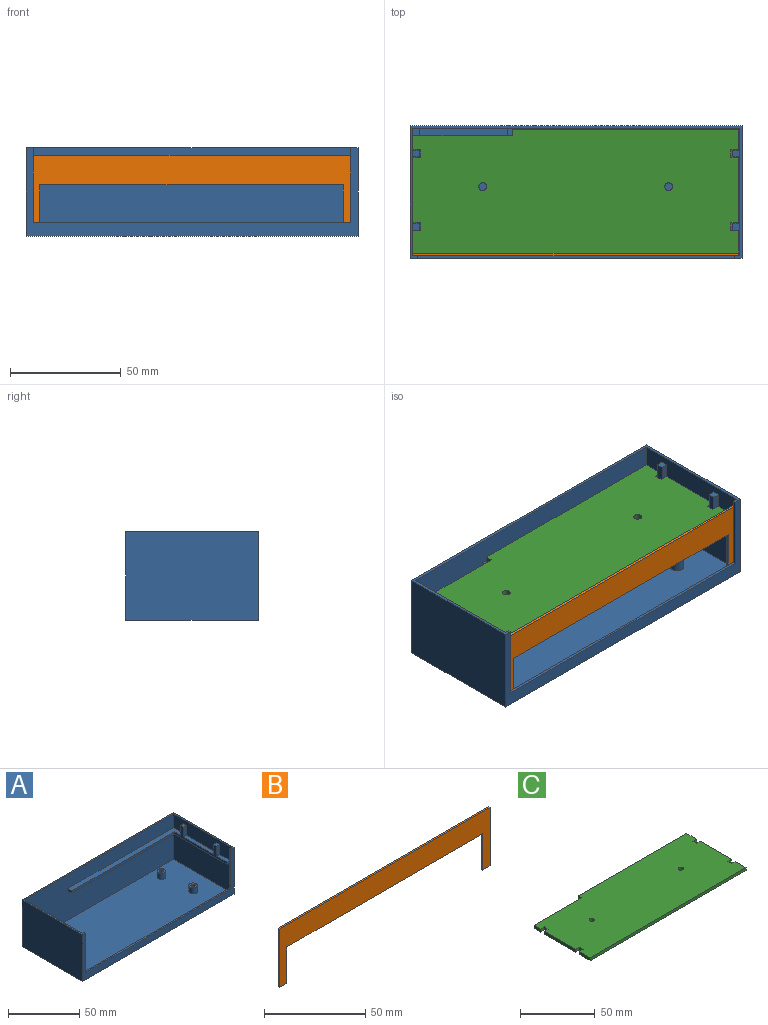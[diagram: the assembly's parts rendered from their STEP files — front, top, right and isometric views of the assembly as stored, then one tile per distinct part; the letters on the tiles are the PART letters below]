
ASSEMBLY  parts=3 mates=4
PART A: 56 faces, bbox 150x60x40 mm
  f0: plane 147.6x57.6mm, normal (0,0,1), area 8388.7mm2, adj f4,f6,f13,f16,f18,f22,f26,f30
  f1: plane 30x3mm, normal (0,0,1), area 90mm2, adj f16,f39,f47,f50
  f2: plane 104.6x10mm, normal (0,0,1), area 436.4mm2, adj f6,f16,f39,f48,f53,f54
  f3: plane 30x3mm, normal (0,0,1), area 90mm2, adj f4,f35,f42,f44
  f4: plane 57.6x38.8mm, normal (1,0,0), area 2071.7mm2, adj f0,f3,f5,f6,f11,f13,f33,f34
  f5: plane 10x3mm, normal (0,0,1), area 30mm2, adj f4,f6,f35,f41
  f6: plane 147.6x38.8mm, normal (0,-1,0), area 5511.7mm2, adj f0,f2,f4,f5,f11,f16,f33,f35
  f7: plane 150x40mm, normal (0,-1,0), area 1146.3mm2, adj f8,f10,f11,f12,f14,f15,f55
  f8: plane 60x40mm, normal (1,0,0), area 2400mm2, adj f7,f9,f11,f12
  f9: plane 150x40mm, normal (0,1,0), area 6000mm2, adj f8,f10,f11,f12
  f10: plane 60x40mm, normal (-1,0,0), area 2400mm2, adj f7,f9,f11,f12
  f11: plane 150x60mm, normal (0,0,1), area 325.9mm2, adj f4,f6,f7,f8,f9,f10,f13,f14
  f12: plane 150x60mm, normal (0,0,-1), area 9000mm2, adj f7,f8,f9,f10
  f13: plane 147.6x38.8mm, normal (0,1,0), area 873.2mm2, adj f0,f4,f11,f14,f15,f16,f55
  f14: plane 33.8x1.2mm, normal (1,0,0), area 40.6mm2, adj f7,f11,f13,f55
  f15: plane 33.8x1.2mm, normal (-1,0,0), area 40.6mm2, adj f7,f11,f13,f55
  f16: plane 57.6x38.8mm, normal (-1,0,0), area 2071.7mm2, adj f0,f1,f2,f6,f11,f13,f37,f38
  f17: cylinder r=1.5mm len=5mm, axis (0,0,-1), area 47.1mm2, adj f19,f20
  f18: cylinder r=3mm len=6mm, axis (0,0,-1), area 94.2mm2, adj f0,f19
  f19: plane 6x6mm, normal (0,0,1), area 21.2mm2, adj f17,f18
  f20: plane 3x3mm, normal (0,0,1), area 7.1mm2, adj f17
  f21: cylinder r=1.5mm len=5mm, axis (0,0,-1), area 47.1mm2, adj f23,f24
  f22: cylinder r=3mm len=6mm, axis (0,0,-1), area 94.2mm2, adj f0,f23
  f23: plane 6x6mm, normal (0,0,1), area 21.2mm2, adj f21,f22
  f24: plane 3x3mm, normal (0,0,1), area 7.1mm2, adj f21
  f25: cylinder r=1.5mm len=5mm, axis (0,0,-1), area 47.1mm2, adj f27,f28
  f26: cylinder r=3mm len=6mm, axis (0,0,-1), area 94.2mm2, adj f0,f27
  f27: plane 6x6mm, normal (0,0,1), area 21.2mm2, adj f25,f26
  f28: plane 3x3mm, normal (0,0,1), area 7.1mm2, adj f25
  f29: cylinder r=1.5mm len=5mm, axis (0,0,-1), area 47.1mm2, adj f31,f32
  f30: cylinder r=3mm len=6mm, axis (0,0,-1), area 94.2mm2, adj f0,f31
  f31: plane 6x6mm, normal (0,0,1), area 21.2mm2, adj f29,f30
  f32: plane 3x3mm, normal (0,0,1), area 7.1mm2, adj f29
  f33: plane 56.1x3mm, normal (0,0,-1), area 168.3mm2, adj f4,f6,f35,f36
  f34: plane 10.1x3mm, normal (0,0,1), area 30.3mm2, adj f4,f35,f36,f45
  f35: plane 56.1x10.5mm, normal (1,0,0), area 163.2mm2, adj f3,f5,f6,f33,f34,f36,f41,f42
  f36: plane 3x2mm, normal (0,-1,0), area 6mm2, adj f4,f33,f34,f35
  f37: plane 104.6x56.1mm, normal (0,0,-1), area 574.7mm2, adj f6,f16,f38,f39,f53,f54
  f38: plane 3x2mm, normal (0,-1,0), area 6mm2, adj f16,f37,f39,f40
  f39: plane 52.1x10.5mm, normal (-1,0,0), area 155.2mm2, adj f1,f2,f37,f38,f40,f47,f48,f49
  f40: plane 10.1x3mm, normal (0,0,1), area 30.3mm2, adj f16,f38,f39,f51
  f41: plane 8.5x3mm, normal (0,1,0), area 25.5mm2, adj f4,f5,f35,f43
  f42: plane 8.5x3mm, normal (0,-1,0), area 25.5mm2, adj f3,f4,f35,f43
  f43: plane 3x3mm, normal (0,0,1), area 9mm2, adj f4,f35,f41,f42
  f44: plane 8.5x3mm, normal (0,1,0), area 25.5mm2, adj f3,f4,f35,f46
  f45: plane 8.5x3mm, normal (0,-1,0), area 25.5mm2, adj f4,f34,f35,f46
  f46: plane 3x3mm, normal (0,0,1), area 9mm2, adj f4,f35,f44,f45
  f47: plane 8.5x3mm, normal (0,-1,0), area 25.5mm2, adj f1,f16,f39,f49
  f48: plane 8.5x3mm, normal (0,1,0), area 25.5mm2, adj f2,f16,f39,f49
  f49: plane 3x3mm, normal (0,0,1), area 9mm2, adj f16,f39,f47,f48
  f50: plane 8.5x3mm, normal (0,1,0), area 25.5mm2, adj f1,f16,f39,f52
  f51: plane 8.5x3mm, normal (0,-1,0), area 25.5mm2, adj f16,f39,f40,f52
  f52: plane 3x3mm, normal (0,0,1), area 9mm2, adj f16,f39,f50,f51
  f53: plane 4x2mm, normal (-1,0,0), area 8mm2, adj f2,f6,f37,f54
  f54: plane 101.6x2mm, normal (0,-1,0), area 203.2mm2, adj f2,f37,f39,f53
  f55: plane 143.6x1.2mm, normal (0,0,1), area 172.3mm2, adj f7,f13,f14,f15
PART B: 10 faces, bbox 147.2x1.2x35.4 mm
  f0: plane 5x1.2mm, normal (0,0,-1), area 6mm2, adj f1,f2,f5,f7
  f1: plane 147.2x35.4mm, normal (0,-1,0), area 2192.5mm2, adj f0,f3,f4,f5,f6,f7,f8,f9
  f2: plane 147.2x35.4mm, normal (0,1,0), area 2192.5mm2, adj f0,f3,f4,f5,f6,f7,f8,f9
  f3: plane 35.4x1.2mm, normal (1,0,0), area 42.5mm2, adj f1,f2,f4,f6
  f4: plane 147.2x1.2mm, normal (0,0,1), area 176.6mm2, adj f1,f2,f3,f5
  f5: plane 35.4x1.2mm, normal (-1,0,0), area 42.5mm2, adj f0,f1,f2,f4
  f6: plane 5x1.2mm, normal (0,0,-1), area 6mm2, adj f1,f2,f3,f8
  f7: plane 22x1.2mm, normal (1,0,0), area 26.4mm2, adj f0,f1,f2,f9
  f8: plane 22x1.2mm, normal (-1,0,0), area 26.4mm2, adj f1,f2,f6,f9
  f9: plane 137.2x1.2mm, normal (0,0,-1), area 164.6mm2, adj f1,f2,f7,f8
PART C: 26 faces, bbox 147.2x56x2.4 mm
  f0: plane 29.5x2.4mm, normal (1,0,0), area 70.8mm2, adj f5,f6,f10,f15
  f1: plane 10.2x2.4mm, normal (1,0,0), area 24.5mm2, adj f5,f6,f9,f12
  f2: plane 6.3x2.4mm, normal (-1,0,0), area 15.1mm2, adj f5,f6,f19,f22
  f3: plane 29.5x2.4mm, normal (-1,0,0), area 70.8mm2, adj f5,f6,f16,f20
  f4: plane 10.2x2.4mm, normal (-1,0,0), area 24.5mm2, adj f5,f6,f9,f17
  f5: plane 147.2x56mm, normal (0,0,1), area 8040mm2, adj f0,f1,f2,f3,f4,f7,f8,f9
  f6: plane 147.2x56mm, normal (0,0,-1), area 8040mm2, adj f0,f1,f2,f3,f4,f7,f8,f9
  f7: plane 9.3x2.4mm, normal (1,0,0), area 22.3mm2, adj f5,f6,f8,f13
  f8: plane 102.2x2.4mm, normal (0,1,0), area 245.3mm2, adj f5,f6,f7,f23
  f9: plane 147.2x2.4mm, normal (0,-1,0), area 353.3mm2, adj f1,f4,f5,f6
  f10: plane 3.5x2.4mm, normal (0,-1,0), area 8.4mm2, adj f0,f5,f6,f11
  f11: plane 3.5x2.4mm, normal (1,0,0), area 8.4mm2, adj f5,f6,f10,f12
  f12: plane 3.5x2.4mm, normal (0,1,0), area 8.4mm2, adj f1,f5,f6,f11
  f13: plane 3.5x2.4mm, normal (0,-1,0), area 8.4mm2, adj f5,f6,f7,f14
  f14: plane 3.5x2.4mm, normal (1,0,0), area 8.4mm2, adj f5,f6,f13,f15
  f15: plane 3.5x2.4mm, normal (0,1,0), area 8.4mm2, adj f0,f5,f6,f14
  f16: plane 3.5x2.4mm, normal (0,-1,0), area 8.4mm2, adj f3,f5,f6,f18
  f17: plane 3.5x2.4mm, normal (0,1,0), area 8.4mm2, adj f4,f5,f6,f18
  f18: plane 3.5x2.4mm, normal (-1,0,0), area 8.4mm2, adj f5,f6,f16,f17
  f19: plane 3.5x2.4mm, normal (0,-1,0), area 8.4mm2, adj f2,f5,f6,f21
  f20: plane 3.5x2.4mm, normal (0,1,0), area 8.4mm2, adj f3,f5,f6,f21
  f21: plane 3.5x2.4mm, normal (-1,0,0), area 8.4mm2, adj f5,f6,f19,f20
  f22: plane 45x2.4mm, normal (0,1,0), area 108mm2, adj f2,f5,f6,f23
  f23: plane 3x2.4mm, normal (-1,0,0), area 7.2mm2, adj f5,f6,f8,f22
  f24: cylinder r=1.75mm len=3.5mm, axis (0,0,1), area 26.4mm2, adj f5,f6
  f25: cylinder r=1.75mm len=3.5mm, axis (0,0,1), area 26.4mm2, adj f5,f6
PLACE A t=(7.8,24.66,12.65)mm fixed
PLACE B t=(7.6,-2.94,31.55)mm
PLACE C t=(7.67,25.06,40.85)mm
MATE planar A.f25 <-> B.f0  axis (0,0,1) through (-44.7,44.16,13.85)mm
MATE planar C.f6 <-> A.f34  axis (0,0,-1) through (8.53,24.61,40.85)mm
MATE planar C.f9 <-> B.f2  axis (0,-1,0) through (7.67,-2.94,42.05)mm
MATE planar B.f1 <-> A.f13  axis (0,-1,0) through (7.6,-4.14,40.77)mm
